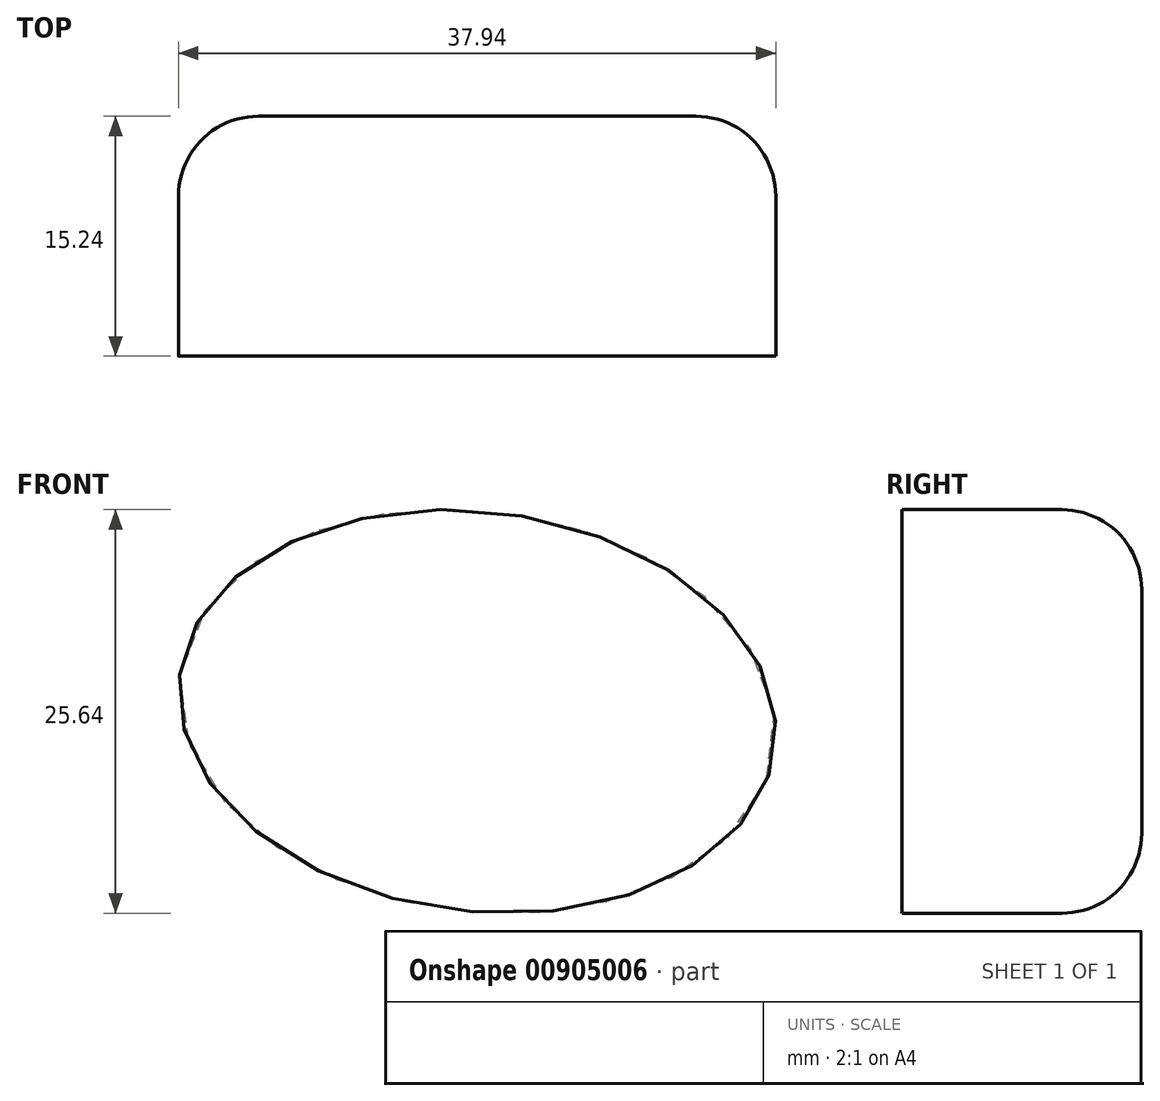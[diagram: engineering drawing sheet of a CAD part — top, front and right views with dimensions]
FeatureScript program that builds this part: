
annotation { "Feature Type Name" : "Feature", "Feature Type Description" : "" }
export const myFeature = defineFeature(function(context is Context, id is Id, definition is map)
    precondition{}
    {
        {
            var Q0;
            Q0=qCreatedBy(makeId("Front.planeOp"),FACE);
            var sketch = newSketch(context, id + "F0", { "sketchPlane" : qUnion([Q0])});
            skEllipse(sketch, "E0", {"center": v(0, 0) * mm, "majorRadius": 19.05 * mm, "minorRadius": 12.7 * mm, "majorAxis": v(-1, 0.12)});
            skSolve(sketch);
        }
        {
            var Q0;
            Q0=makeQuery(id+"F0.imprint","IMPRINT",FACE,{"disambiguationData":[TD([[makeQuery(id+"F0.imprint","IMPRINT",EDGE,{"derivedFrom":sQuery(id+"F0.wireOp",EDGE,"E0")}),1.0]])]});
            extrude(context, id + "F1", {"entities" : qUnion([Q0]), "depth" : 5.08 * mm, "offsetDistance" : 25.4 * mm});
        }
        {
            var Q0;
            Q0=makeQuery(id+"F1.opExtrude","CAP_FACE",FACE,{"disambiguationData":[OSD([sQuery(id+"F0.wireOp",EDGE,"E0")])],"isStart":true});
            extrude(context, id + "F2", {"entities" : qUnion([Q0]), "operationType" : NewBodyOperationType.ADD, "depth" : 2.54 * mm, "offsetDistance" : 25.4 * mm});
        }
        {
            var Q0;
            Q0=makeQuery(id+"F2.opExtrude","CAP_FACE",FACE,{"disambiguationData":[OSD([sQuery(id+"F0.wireOp",EDGE,"E0")])],"isStart":false});
            extrude(context, id + "F3", {"entities" : qUnion([Q0]), "operationType" : NewBodyOperationType.ADD, "depth" : 7.62 * mm, "offsetDistance" : 25.4 * mm});
        }
        {
            var Q0;
            Q0=makeQuery(id+"F3.opExtrude","CAP_EDGE",EDGE,{"disambiguationData":[OSD([sQuery(id+"F0.wireOp",EDGE,"E0")])],"isStart":false});
            fillet(context, id + "F4", {"entities" : qUnion([Q0]), "radius" : 5.08 * mm, "tangentPropagation" : true, "allowEdgeOverflow" : false});
        }
    });
